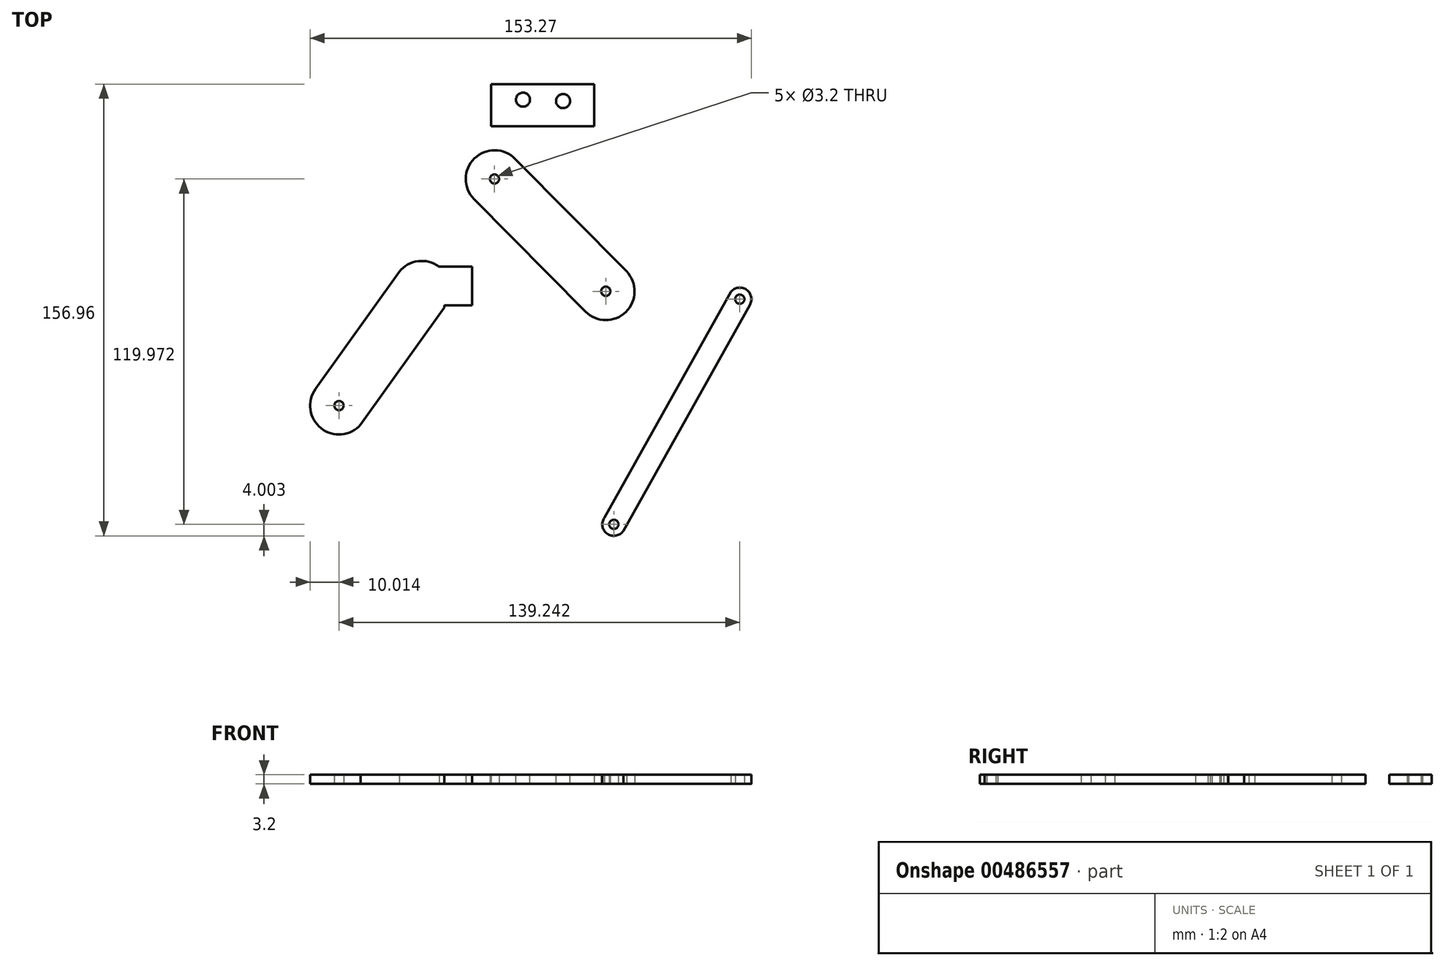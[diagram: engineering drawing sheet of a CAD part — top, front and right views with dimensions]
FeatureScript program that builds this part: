
annotation { "Feature Type Name" : "Feature", "Feature Type Description" : "" }
export const myFeature = defineFeature(function(context is Context, id is Id, definition is map)
    precondition{}
    {
        {
            var Q0;
            Q0=qCreatedBy(makeId("Top.planeOp"),FACE);
            var sketch = newSketch(context, id + "F0", { "sketchPlane" : qUnion([Q0])});
            skLineSegment(sketch, "E0", {"start": v(12.2, -26.52) * mm, "end": v(-26.5, 12.54) * mm});
            skLineSegment(sketch, "E1", {"start": v(-12.17, 26.49) * mm, "end": v(26.54, -12.58) * mm});
            skArc(sketch, "E2", {"start": v(12.2, -26.52) * mm, "mid": v(26.28, -26.65) * mm, "end": v(26.54, -12.58) * mm});
            skArc(sketch, "E3", {"start": v(-12.17, 26.49) * mm, "mid": v(-26.31, 26.68) * mm, "end": v(-26.5, 12.54) * mm});
            skCircle(sketch, "E4", {"center": v(19.3, -19.48) * mm, "radius": 1.6 * mm});
            skCircle(sketch, "E5", {"center": v(-19.34, 19.52) * mm, "radius": 1.6 * mm});
            skSolve(sketch);
        }
        {
            var Q0;
            Q0=qCreatedBy(makeId("Top.planeOp"),FACE);
            var sketch = newSketch(context, id + "F1", { "sketchPlane" : qUnion([Q0])});
            skLineSegment(sketch, "E6", {"start": v(-81.52, -53.39) * mm, "end": v(-52.41, -12.73) * mm});
            skLineSegment(sketch, "E7", {"start": v(-36.73, -25.14) * mm, "end": v(-65.83, -65.8) * mm});
            skArc(sketch, "E8", {"start": v(-81.52, -53.39) * mm, "mid": v(-79.59, -67.07) * mm, "end": v(-65.83, -65.8) * mm});
            skCircle(sketch, "E9", {"center": v(-73.38, -59.22) * mm, "radius": 1.6 * mm});
            skArc(sketch, "E10", {"start": v(-36.73, -25.14) * mm, "mid": v(-38.36, -11.1) * mm, "end": v(-52.41, -12.73) * mm});
            skLineSegment(sketch, "E11", {"start": v(-38.39, -11.07) * mm, "end": v(-36.8, -25.25) * mm});
            skSolve(sketch);
        }
        {
            var Q0;
            Q0 = qSketchRegion(id + "F1", true);
            extrude(context, id + "F2", {"entities" : qUnion([Q0]), "depth" : 3.2 * mm, "offsetDistance" : 25 * mm});
        }
        {
            var Q0;
            Q0=makeQuery(id+"F2.opExtrude","CAP_FACE",FACE,{"disambiguationData":[OSD([sQuery(id+"F1.wireOp",EDGE,"E6"),sQuery(id+"F1.wireOp",EDGE,"E7"),sQuery(id+"F1.wireOp",EDGE,"E8"),sQuery(id+"F1.wireOp",EDGE,"E9"),sQuery(id+"F1.wireOp",EDGE,"E10")])],"isStart":false});
            var sketch = newSketch(context, id + "F3", { "sketchPlane" : qUnion([Q0])});
            skLineSegment(sketch, "E12", {"start": v(-38.36, -11.1) * mm, "end": v(-36.73, -25.14) * mm});
            skFitSpline(sketch, "E13", {"points": [v(-38.36, -11.1) * mm, v(-33.37, -14.28) * mm, v(-31.28, -21.73) * mm, v(-36.73, -25.14) * mm], "startDerivative": vector(16.94, -6.8) * mm, "endDerivative": vector(-21.72, -7.06) * mm});
            skSolve(sketch);
        }
        {
            var Q0;
            Q0 = qSketchRegion(id + "F3", true);
            extrude(context, id + "F4", {"entities" : qUnion([Q0]), "operationType" : NewBodyOperationType.REMOVE, "oppositeDirection" : true, "depth" : 25 * mm, "offsetDistance" : 25 * mm});
        }
        {
            var Q0;
            Q0=qCreatedBy(makeId("Top.planeOp"),FACE);
            var sketch = newSketch(context, id + "F5", { "sketchPlane" : qUnion([Q0])});
            skLineSegment(sketch, "E14", {"start": v(69.37, -24.2) * mm, "end": v(25.4, -102.72) * mm});
            skLineSegment(sketch, "E15", {"start": v(18.8, -98.2) * mm, "end": v(62.78, -19.66) * mm});
            skArc(sketch, "E16", {"start": v(69.37, -24.2) * mm, "mid": v(68.14, -18.92) * mm, "end": v(62.78, -19.66) * mm});
            skArc(sketch, "E17", {"start": v(18.8, -98.2) * mm, "mid": v(19.84, -103.75) * mm, "end": v(25.4, -102.72) * mm});
            skCircle(sketch, "E18", {"center": v(65.87, -22.23) * mm, "radius": 1.6 * mm});
            skCircle(sketch, "E19", {"center": v(22.1, -100.46) * mm, "radius": 1.6 * mm});
            skSolve(sketch);
        }
        {
            var Q0;
            Q0 = qSketchRegion(id + "F5", true);
            extrude(context, id + "F6", {"entities" : qUnion([Q0]), "depth" : 3.2 * mm, "offsetDistance" : 25 * mm});
        }
        {
            var Q0;
            Q0=qCreatedBy(makeId("Top.planeOp"),FACE);
            var sketch = newSketch(context, id + "F7", { "sketchPlane" : qUnion([Q0])});
            skLineSegment(sketch, "E20.bottom", {"start": v(-20.58, 52.5) * mm, "end": v(15.27, 52.5) * mm});
            skLineSegment(sketch, "E20.top", {"start": v(-20.58, 37.84) * mm, "end": v(15.27, 37.84) * mm});
            skLineSegment(sketch, "E20.left", {"start": v(-20.58, 52.5) * mm, "end": v(-20.58, 37.84) * mm});
            skLineSegment(sketch, "E20.right", {"start": v(15.27, 52.5) * mm, "end": v(15.27, 37.84) * mm});
            skSolve(sketch);
        }
        {
            var Q0;
            Q0 = qSketchRegion(id + "F7", true);
            extrude(context, id + "F8", {"entities" : qUnion([Q0]), "depth" : 3.2 * mm, "offsetDistance" : 25 * mm});
        }
        {
            var Q0;
            Q0=makeQuery(id+"F8.opExtrude","CAP_FACE",FACE,{"disambiguationData":[OSD([sQuery(id+"F7.wireOp",EDGE,"E20.bottom"),sQuery(id+"F7.wireOp",EDGE,"E20.top"),sQuery(id+"F7.wireOp",EDGE,"E20.left"),sQuery(id+"F7.wireOp",EDGE,"E20.right")])],"isStart":false});
            var sketch = newSketch(context, id + "F9", { "sketchPlane" : qUnion([Q0])});
            skCircle(sketch, "E21", {"center": v(-9.45, 47.1) * mm, "radius": 2.44 * mm});
            skSolve(sketch);
        }
        {
            var Q0;
            Q0 = qSketchRegion(id + "F9", true);
            extrude(context, id + "F10", {"entities" : qUnion([Q0]), "operationType" : NewBodyOperationType.REMOVE, "oppositeDirection" : true, "depth" : 25 * mm, "offsetDistance" : 25 * mm});
        }
        {
            var Q0;
            Q0 = qSketchRegion(id + "F0", true);
            extrude(context, id + "F11", {"entities" : qUnion([Q0]), "depth" : 3.2 * mm, "offsetDistance" : 25 * mm});
        }
        {
            var Q0;
            Q0=makeQuery(id+"F8.opExtrude","CAP_FACE",FACE,{"disambiguationData":[OSD([sQuery(id+"F7.wireOp",EDGE,"E20.bottom"),sQuery(id+"F7.wireOp",EDGE,"E20.top"),sQuery(id+"F7.wireOp",EDGE,"E20.left"),sQuery(id+"F7.wireOp",EDGE,"E20.right")])],"isStart":false});
            var sketch = newSketch(context, id + "F12", { "sketchPlane" : qUnion([Q0])});
            skCircle(sketch, "E22", {"center": v(4.46, 46.6) * mm, "radius": 2.44 * mm});
            skSolve(sketch);
        }
        {
            var Q0;
            Q0 = qSketchRegion(id + "F12", true);
            extrude(context, id + "F13", {"entities" : qUnion([Q0]), "operationType" : NewBodyOperationType.REMOVE, "oppositeDirection" : true, "depth" : 3.2 * mm, "offsetDistance" : 25 * mm});
        }
        {
            var Q0;
            Q0=qCreatedBy(makeId("Top.planeOp"),FACE);
            var sketch = newSketch(context, id + "F14", { "sketchPlane" : qUnion([Q0])});
            skLineSegment(sketch, "E23.bottom", {"start": v(-40.65, -24.4) * mm, "end": v(-27.16, -24.4) * mm});
            skLineSegment(sketch, "E23.top", {"start": v(-40.65, -10.92) * mm, "end": v(-27.16, -10.92) * mm});
            skLineSegment(sketch, "E23.left", {"start": v(-40.65, -24.4) * mm, "end": v(-40.65, -10.92) * mm});
            skLineSegment(sketch, "E23.right", {"start": v(-27.16, -24.4) * mm, "end": v(-27.16, -10.92) * mm});
            skSolve(sketch);
        }
        {
            var Q0;
            Q0 = qSketchRegion(id + "F14", true);
            extrude(context, id + "F15", {"entities" : qUnion([Q0]), "operationType" : NewBodyOperationType.ADD, "depth" : 3.2 * mm, "offsetDistance" : 25 * mm});
        }
    });
